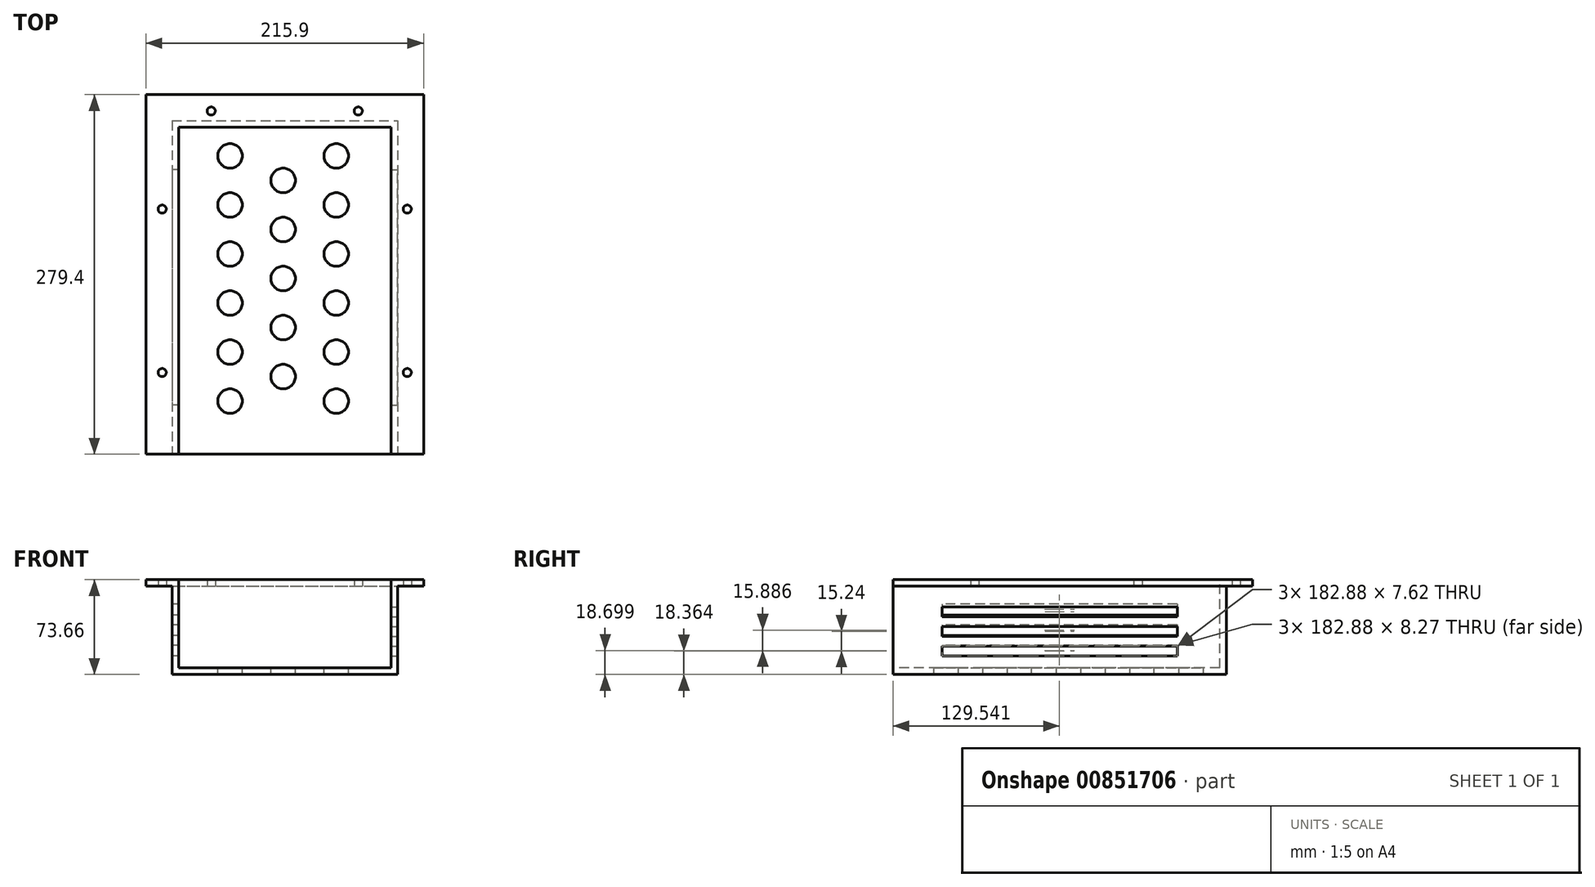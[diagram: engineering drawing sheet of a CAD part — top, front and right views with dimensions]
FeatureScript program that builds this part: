
annotation { "Feature Type Name" : "Feature", "Feature Type Description" : "" }
export const myFeature = defineFeature(function(context is Context, id is Id, definition is map)
    precondition{}
    {
        {
            var Q0;
            Q0=qCreatedBy(makeId("Top.planeOp"),FACE);
            var sketch = newSketch(context, id + "F0", { "sketchPlane" : qUnion([Q0])});
            skLineSegment(sketch, "E0.bottom", {"start": v(-81.34, 128.3) * mm, "end": v(83.76, 128.3) * mm});
            skLineSegment(sketch, "E0.top", {"start": v(-81.34, -125.7) * mm, "end": v(83.76, -125.7) * mm});
            skLineSegment(sketch, "E0.left", {"start": v(-81.34, 128.3) * mm, "end": v(-81.34, -125.7) * mm});
            skLineSegment(sketch, "E0.right", {"start": v(83.76, 128.3) * mm, "end": v(83.76, -125.7) * mm});
            skLineSegment(sketch, "E1.bottom", {"start": v(-81.34, 128.3) * mm, "end": v(-106.74, 128.3) * mm});
            skLineSegment(sketch, "E1.top", {"start": v(-81.34, -125.7) * mm, "end": v(-106.74, -125.7) * mm});
            skLineSegment(sketch, "E1.right", {"start": v(-106.74, 128.3) * mm, "end": v(-106.74, -125.7) * mm});
            skLineSegment(sketch, "E2.bottom", {"start": v(83.76, 128.3) * mm, "end": v(109.16, 128.3) * mm});
            skLineSegment(sketch, "E2.top", {"start": v(83.76, -125.7) * mm, "end": v(109.16, -125.7) * mm});
            skLineSegment(sketch, "E2.right", {"start": v(109.16, 128.3) * mm, "end": v(109.16, -125.7) * mm});
            skLineSegment(sketch, "E3.bottom", {"start": v(-106.74, 128.3) * mm, "end": v(109.16, 128.3) * mm});
            skLineSegment(sketch, "E3.top", {"start": v(-106.74, 153.7) * mm, "end": v(109.16, 153.7) * mm});
            skLineSegment(sketch, "E3.left", {"start": v(-106.74, 128.3) * mm, "end": v(-106.74, 153.7) * mm});
            skLineSegment(sketch, "E3.right", {"start": v(109.16, 128.3) * mm, "end": v(109.16, 153.7) * mm});
            skSolve(sketch);
        }
        {
            var Q0;
            Q0=makeQuery(id+"F0.imprint","IMPRINT",FACE,{"disambiguationData":[TD([[makeQuery(id+"F0.imprint","IMPRINT",EDGE,{"derivedFrom":sQuery(id+"F0.wireOp",EDGE,"E0.bottom")}),-1.0]])]});
            extrude(context, id + "F1", {"entities" : qUnion([Q0]), "oppositeDirection" : true, "depth" : 63.5 * mm, "offsetDistance" : 25.4 * mm});
        }
        {
            var Q0;
            Q0=makeQuery(id+"F1.opExtrude","SWEPT_FACE",FACE,{"disambiguationData":[OSD([sQuery(id+"F0.wireOp",EDGE,"E0.top")])]});
            var Q1;
            Q1=makeQuery(id+"F1.opExtrude","CAP_FACE",FACE,{"disambiguationData":[OSD([sQuery(id+"F0.wireOp",EDGE,"E0.bottom"),sQuery(id+"F0.wireOp",EDGE,"E0.top"),sQuery(id+"F0.wireOp",EDGE,"E0.left"),sQuery(id+"F0.wireOp",EDGE,"E0.right")])],"isStart":true});
            var Q2;
            Q2=makeQuery(id+"F1.opExtrude","SWEPT_BODY",BODY,{"disambiguationData":[OSD([sQuery(id+"F0.wireOp",EDGE,"E0.bottom"),sQuery(id+"F0.wireOp",EDGE,"E0.top"),sQuery(id+"F0.wireOp",EDGE,"E0.left"),sQuery(id+"F0.wireOp",EDGE,"E0.right")])]});
            shell(context, id + "F2", {"entities" : qUnion([Q0, Q1]), "parts" : qUnion([Q2]), "thickness" : 5.08 * mm, "oppositeDirection" : true});
        }
        {
            var Q0;
            Q0=makeQuery(id+"F0.imprint","IMPRINT",FACE,{"disambiguationData":[TD([[makeQuery(id+"F0.imprint","IMPRINT",EDGE,{"derivedFrom":sQuery(id+"F0.wireOp",EDGE,"E0.left")}),-1.0]])]});
            var Q1;
            Q1=makeQuery(id+"F0.imprint","IMPRINT",FACE,{"disambiguationData":[TD([[makeQuery(id+"F0.imprint","IMPRINT",EDGE,{"derivedFrom":sQuery(id+"F0.wireOp",EDGE,"E0.bottom")}),1.0]])]});
            var Q2;
            Q2=makeQuery(id+"F0.imprint","IMPRINT",FACE,{"disambiguationData":[TD([[makeQuery(id+"F0.imprint","IMPRINT",EDGE,{"derivedFrom":sQuery(id+"F0.wireOp",EDGE,"E0.right")}),1.0]])]});
            extrude(context, id + "F3", {"entities" : qUnion([Q0, Q1, Q2]), "operationType" : NewBodyOperationType.ADD, "depth" : 5.08 * mm, "offsetDistance" : 25.4 * mm});
        }
        {
            var Q0;
            Q0=makeQuery(id+"F0.imprint","IMPRINT",FACE,{"disambiguationData":[TD([[makeQuery(id+"F0.imprint","IMPRINT",EDGE,{"derivedFrom":sQuery(id+"F0.wireOp",EDGE,"E0.left")}),-1.0]])]});
            var sketch = newSketch(context, id + "F4", { "sketchPlane" : qUnion([Q0])});
            skCircle(sketch, "E4", {"center": v(-94.04, -62.2) * mm, "radius": 6.5 * mm});
            skCircle(sketch, "E5", {"center": v(-94.04, 64.8) * mm, "radius": 6.5 * mm});
            skCircle(sketch, "E6", {"center": v(-55.94, 141) * mm, "radius": 6.5 * mm});
            skCircle(sketch, "E7", {"center": v(58.36, 141) * mm, "radius": 6.5 * mm});
            skCircle(sketch, "E8", {"center": v(96.46, 64.8) * mm, "radius": 6.5 * mm});
            skCircle(sketch, "E9", {"center": v(96.46, -62.2) * mm, "radius": 6.5 * mm});
            skSolve(sketch);
        }
        {
            var Q0;
            Q0=sQuery(id+"F4.wireOp",VERTEX,"E5.center");
            var Q1;
            Q1=sQuery(id+"F4.wireOp",VERTEX,"E4.center");
            var Q2;
            Q2=sQuery(id+"F4.wireOp",VERTEX,"E6.center");
            var Q3;
            Q3=sQuery(id+"F4.wireOp",VERTEX,"E9.center");
            var Q4;
            Q4=sQuery(id+"F4.wireOp",VERTEX,"E8.center");
            var Q5;
            Q5=sQuery(id+"F4.wireOp",VERTEX,"E7.center");
            var Q6;
            Q6=makeQuery(id+"F1.opExtrude","SWEPT_BODY",BODY,{"disambiguationData":[OSD([sQuery(id+"F0.wireOp",EDGE,"E0.bottom"),sQuery(id+"F0.wireOp",EDGE,"E0.top"),sQuery(id+"F0.wireOp",EDGE,"E0.left"),sQuery(id+"F0.wireOp",EDGE,"E0.right")])]});
            hole(context, id + "F5", {"style" : HoleStyle.SIMPLE, "endStyle" : HoleEndStyle.THROUGH, "oppositeDirection" : true, "holeDiameter" : 6.35 * mm, "majorDiameter" : 6.35 * mm, "tappedDepth" : 12.7 * mm, "tapClearance" : 3, "startFromSketch" : true, "locations" : qUnion([Q0, Q1, Q2, Q3, Q4, Q5]), "scope" : qUnion([Q6])});
        }
        {
            var Q0;
            Q0=makeQuery(id+"F2.opShell","OFFSET_FACE",FACE,{"disambiguationData":[OSD([sQuery(id+"F0.wireOp",EDGE,"E0.bottom"),sQuery(id+"F0.wireOp",EDGE,"E0.top"),sQuery(id+"F0.wireOp",EDGE,"E0.left"),sQuery(id+"F0.wireOp",EDGE,"E0.right")])]});
            var sketch = newSketch(context, id + "F6", { "sketchPlane" : qUnion([Q0])});
            skCircle(sketch, "E10", {"center": v(-41.27, 106.08) * mm, "radius": 9.53 * mm});
            skCircle(sketch, "E11", {"center": v(0, 87.03) * mm, "radius": 9.53 * mm});
            skCircle(sketch, "E12", {"center": v(41.28, 106.08) * mm, "radius": 9.53 * mm});
            skCircle(sketch, "E13", {"center": v(41.28, 67.98) * mm, "radius": 9.53 * mm});
            skCircle(sketch, "E14", {"center": v(-41.27, 67.98) * mm, "radius": 9.53 * mm});
            skCircle(sketch, "E15", {"center": v(0, 48.93) * mm, "radius": 9.53 * mm});
            skCircle(sketch, "E16", {"center": v(41.28, 29.88) * mm, "radius": 9.53 * mm});
            skCircle(sketch, "E17", {"center": v(-41.27, 29.88) * mm, "radius": 9.53 * mm});
            skCircle(sketch, "E18", {"center": v(-41.27, -8.22) * mm, "radius": 9.53 * mm});
            skCircle(sketch, "E19", {"center": v(41.28, -8.22) * mm, "radius": 9.53 * mm});
            skCircle(sketch, "E20", {"center": v(0, 10.83) * mm, "radius": 9.53 * mm});
            skCircle(sketch, "E21", {"center": v(0, -27.27) * mm, "radius": 9.53 * mm});
            skCircle(sketch, "E22", {"center": v(-41.27, -46.32) * mm, "radius": 9.53 * mm});
            skCircle(sketch, "E23", {"center": v(41.28, -46.32) * mm, "radius": 9.53 * mm});
            skCircle(sketch, "E24", {"center": v(0, -65.37) * mm, "radius": 9.53 * mm});
            skCircle(sketch, "E25", {"center": v(-41.27, -84.42) * mm, "radius": 9.53 * mm});
            skCircle(sketch, "E26", {"center": v(41.28, -84.42) * mm, "radius": 9.53 * mm});
            skSolve(sketch);
        }
        {
            var Q0;
            Q0=sQuery(id+"F6.wireOp",VERTEX,"E10.center");
            var Q1;
            Q1=sQuery(id+"F6.wireOp",VERTEX,"E12.center");
            var Q2;
            Q2=sQuery(id+"F6.wireOp",VERTEX,"E13.center");
            var Q3;
            Q3=sQuery(id+"F6.wireOp",VERTEX,"E11.center");
            var Q4;
            Q4=sQuery(id+"F6.wireOp",VERTEX,"E14.center");
            var Q5;
            Q5=sQuery(id+"F6.wireOp",VERTEX,"E15.center");
            var Q6;
            Q6=sQuery(id+"F6.wireOp",VERTEX,"E16.center");
            var Q7;
            Q7=sQuery(id+"F6.wireOp",VERTEX,"E17.center");
            var Q8;
            Q8=sQuery(id+"F6.wireOp",VERTEX,"E20.center");
            var Q9;
            Q9=sQuery(id+"F6.wireOp",VERTEX,"E18.center");
            var Q10;
            Q10=sQuery(id+"F6.wireOp",VERTEX,"E19.center");
            var Q11;
            Q11=sQuery(id+"F6.wireOp",VERTEX,"E21.center");
            var Q12;
            Q12=sQuery(id+"F6.wireOp",VERTEX,"E23.center");
            var Q13;
            Q13=sQuery(id+"F6.wireOp",VERTEX,"E22.center");
            var Q14;
            Q14=sQuery(id+"F6.wireOp",VERTEX,"E24.center");
            var Q15;
            Q15=sQuery(id+"F6.wireOp",VERTEX,"E26.center");
            var Q16;
            Q16=sQuery(id+"F6.wireOp",VERTEX,"E25.center");
            var Q17;
            Q17=makeQuery(id+"F1.opExtrude","SWEPT_BODY",BODY,{"disambiguationData":[OSD([sQuery(id+"F0.wireOp",EDGE,"E0.bottom"),sQuery(id+"F0.wireOp",EDGE,"E0.top"),sQuery(id+"F0.wireOp",EDGE,"E0.left"),sQuery(id+"F0.wireOp",EDGE,"E0.right")])]});
            hole(context, id + "F7", {"style" : HoleStyle.SIMPLE, "endStyle" : HoleEndStyle.THROUGH, "holeDiameter" : 19.05 * mm, "majorDiameter" : 6.35 * mm, "tappedDepth" : 12.7 * mm, "tapClearance" : 3, "startFromSketch" : true, "locations" : qUnion([Q0, Q1, Q2, Q3, Q4, Q5, Q6, Q7, Q8, Q9, Q10, Q11, Q12, Q13, Q14, Q15, Q16]), "scope" : qUnion([Q17])});
        }
        {
            var Q0;
            Q0=makeQuery(id+"F1.opExtrude","SWEPT_FACE",FACE,{"disambiguationData":[OSD([sQuery(id+"F0.wireOp",EDGE,"E0.left")])]});
            var sketch = newSketch(context, id + "F8", { "sketchPlane" : qUnion([Q0])});
            skLineSegment(sketch, "E27.bottom", {"start": v(-95.28, -13.97) * mm, "end": v(87.6, -13.97) * mm});
            skLineSegment(sketch, "E27.top", {"start": v(-95.28, -22.24) * mm, "end": v(87.6, -22.24) * mm});
            skLineSegment(sketch, "E27.left", {"start": v(-95.28, -13.97) * mm, "end": v(-95.28, -22.24) * mm});
            skLineSegment(sketch, "E27.right", {"start": v(87.6, -13.97) * mm, "end": v(87.6, -22.24) * mm});
            skLineSegment(sketch, "E28.bottom", {"start": v(-95.28, -29.86) * mm, "end": v(87.6, -29.86) * mm});
            skLineSegment(sketch, "E28.top", {"start": v(-95.28, -38.13) * mm, "end": v(87.6, -38.13) * mm});
            skLineSegment(sketch, "E28.left", {"start": v(-95.28, -29.86) * mm, "end": v(-95.28, -38.13) * mm});
            skLineSegment(sketch, "E28.right", {"start": v(87.6, -29.86) * mm, "end": v(87.6, -38.13) * mm});
            skLineSegment(sketch, "E29.bottom", {"start": v(-95.28, -45.75) * mm, "end": v(87.6, -45.75) * mm});
            skLineSegment(sketch, "E29.top", {"start": v(-95.28, -54.01) * mm, "end": v(87.6, -54.01) * mm});
            skLineSegment(sketch, "E29.left", {"start": v(-95.28, -45.75) * mm, "end": v(-95.28, -54.01) * mm});
            skLineSegment(sketch, "E29.right", {"start": v(87.6, -45.75) * mm, "end": v(87.6, -54.01) * mm});
            skSolve(sketch);
        }
        {
            var Q0;
            Q0=makeQuery(id+"F8.imprint","IMPRINT",FACE,{"disambiguationData":[TD([[makeQuery(id+"F8.imprint","IMPRINT",EDGE,{"derivedFrom":sQuery(id+"F8.wireOp",EDGE,"E27.bottom")}),-1.0]])]});
            var Q1;
            Q1=makeQuery(id+"F8.imprint","IMPRINT",FACE,{"disambiguationData":[TD([[makeQuery(id+"F8.imprint","IMPRINT",EDGE,{"derivedFrom":sQuery(id+"F8.wireOp",EDGE,"E28.bottom")}),-1.0]])]});
            var Q2;
            Q2=makeQuery(id+"F8.imprint","IMPRINT",FACE,{"disambiguationData":[TD([[makeQuery(id+"F8.imprint","IMPRINT",EDGE,{"derivedFrom":sQuery(id+"F8.wireOp",EDGE,"E29.bottom")}),-1.0]])]});
            extrude(context, id + "F9", {"entities" : qUnion([Q0, Q1, Q2]), "operationType" : NewBodyOperationType.REMOVE, "oppositeDirection" : true, "depth" : 25.4 * mm, "offsetDistance" : 25.4 * mm});
        }
        {
            var Q0;
            Q0=makeQuery(id+"F1.opExtrude","SWEPT_FACE",FACE,{"disambiguationData":[OSD([sQuery(id+"F0.wireOp",EDGE,"E0.right")])]});
            var sketch = newSketch(context, id + "F10", { "sketchPlane" : qUnion([Q0])});
            skLineSegment(sketch, "E30.bottom", {"start": v(-87.6, -15.93) * mm, "end": v(95.28, -15.93) * mm});
            skLineSegment(sketch, "E30.top", {"start": v(-87.6, -23.55) * mm, "end": v(95.28, -23.55) * mm});
            skLineSegment(sketch, "E30.left", {"start": v(-87.6, -15.93) * mm, "end": v(-87.6, -23.55) * mm});
            skLineSegment(sketch, "E30.right", {"start": v(95.28, -15.93) * mm, "end": v(95.28, -23.55) * mm});
            skLineSegment(sketch, "E31.bottom", {"start": v(-87.6, -31.17) * mm, "end": v(95.28, -31.17) * mm});
            skLineSegment(sketch, "E31.top", {"start": v(-87.6, -38.79) * mm, "end": v(95.28, -38.79) * mm});
            skLineSegment(sketch, "E31.left", {"start": v(-87.6, -31.17) * mm, "end": v(-87.6, -38.79) * mm});
            skLineSegment(sketch, "E31.right", {"start": v(95.28, -31.17) * mm, "end": v(95.28, -38.79) * mm});
            skLineSegment(sketch, "E32.bottom", {"start": v(-87.6, -46.4) * mm, "end": v(95.28, -46.4) * mm});
            skLineSegment(sketch, "E32.top", {"start": v(-87.6, -54.03) * mm, "end": v(95.28, -54.03) * mm});
            skLineSegment(sketch, "E32.left", {"start": v(-87.6, -46.4) * mm, "end": v(-87.6, -54.03) * mm});
            skLineSegment(sketch, "E32.right", {"start": v(95.28, -46.4) * mm, "end": v(95.28, -54.03) * mm});
            skSolve(sketch);
        }
        {
            var Q0;
            Q0=makeQuery(id+"F10.imprint","IMPRINT",FACE,{"disambiguationData":[TD([[makeQuery(id+"F10.imprint","IMPRINT",EDGE,{"derivedFrom":sQuery(id+"F10.wireOp",EDGE,"E30.bottom")}),-1.0]])]});
            var Q1;
            Q1=makeQuery(id+"F10.imprint","IMPRINT",FACE,{"disambiguationData":[TD([[makeQuery(id+"F10.imprint","IMPRINT",EDGE,{"derivedFrom":sQuery(id+"F10.wireOp",EDGE,"E31.bottom")}),-1.0]])]});
            var Q2;
            Q2=makeQuery(id+"F10.imprint","IMPRINT",FACE,{"disambiguationData":[TD([[makeQuery(id+"F10.imprint","IMPRINT",EDGE,{"derivedFrom":sQuery(id+"F10.wireOp",EDGE,"E32.bottom")}),-1.0]])]});
            extrude(context, id + "F11", {"entities" : qUnion([Q0, Q1, Q2]), "operationType" : NewBodyOperationType.REMOVE, "oppositeDirection" : true, "depth" : 25.4 * mm, "offsetDistance" : 25.4 * mm});
        }
    });
